# Revit family: Hager-PEDRO-Surface_mounted-IP66-With_Cover-With_DIN-NoHosted-IT-it
name_source: partatom
category: Electrical Equipment
units: mm (PartAtom-declared; Revit-internal decimal feet)

## family parameters
Always vertical = Yes
Cut with Voids When Loaded = No
Maintain Annotation Orientation = No
Panel Configuration = Two Columns, Circuits Across
Part Type = Panelboard
Room Calculation Point = No
Round Connector Dimension = Use Diameter
Shared = No
Work Plane-Based = Yes

## types (26) — shared parameters
Code hager = ADD-EC000214_EU
Default Elevation = 1200 mm
EF000003 - Tipo di montaggio = A parete
EF000007 - Colore = Grigio
EF000024 - Resistente ai raggi UV = No
EF000116 - Numero RAL = 7035
EF000118 - Con piastra di montaggio = No
EF001062 - Esecuzione EMC = Yes
EF001088 - Possibilità di applicazione = Yes
EF001134 - Barra DIN = Yes
EF004462 - Tipo di chiusura = Altro
EF005474 - Grado di protezione (IP) = IP66
EF006306 - Con serratura = Yes
EF009212 - Esecuzione coperchio = Chiuso
EF015776 - Morsettiera di terra = No
EF015777 - Morsettiera neutra = No
EF015941 - Segnale di passaggio porta = No
ETIM class code = EC000214
ETIM class name = Small distribution board
HG000002-with door or cover-it = Yes
HG000003-Range-it = PEDRO
HG000005-Thickness-it = 2 mm  [stored 0.00656168 ft]
HG000006-Flush mounted-it = No
HG000009-Double swing door-it = No
HG000010-Asymmetric doors-it = No
HG000011-Empty rows from bottom-it = No
HG000012-Door swing angle-it = 90.00°
HG000013-Door on the left-it = No
HG000014-Door on the right-it = Yes
HG000015-Clearance visibility-it = Yes
HG000016-Door 3D visibility-it = Yes
HG000017-Distance between poles-it = 18 mm  [stored 0.0590551 ft]
HG000060-RAL-number = 7035
HG000099-Onfly Template ID-it-IT = 507532
Manufacturer = Hager
Name BIM&CO = Electricity
Name hager = ADD_Enclosures_EC000214
Reference = Template-Enclosure_EU-EC000214
Uniformat = Low Tension Service & Dist.
Uniformat code = D501001
zero-valued in all types: EF000218 - Profondità di incasso, EF000332 - Altezza della parte incassata, EF000846 - Larghezza di montaggio, EF001131 - Profondità interna, HG000007-Number of empty columns-it, HG000008-Number of empty rows-it

## per-type parameters (varying)
| type | BC_METADATA | EF000008 - Larghezza | EF000040 - Altezza | EF000049 - Profondità | EF000266 - Numero di file | EF002950 - Numero moduli DIN | EF006244 - Coperchio/porta trasparente | HG000001 - Numero di colonne | HG000004-Manufacturer reference-it | HGEF000266-Numero di file | HGEF0002950-Numero moduli DIN |
| PEDRO-Surface_mounted_W265_H303_D167_0_Modular_Spacing-B04601 | {"ObjectGuid":"712c051a-f6a5-42ba-8971-c6f35d6c2ee9","ModelGuid":"f9864149-d723-4e03-9b42-689d61447cad","VariantGuid":"83e1c283-c7cc-4c8f-adfe-bcd37362c99a","Revision":"#6","VariantName":"PEDRO-Surface_mounted_W265_H303_D167_0_Modular_Spacing-B04601"} | 265 mm  [stored 0.869423 ft] | 303 mm  [stored 0.994094 ft] | 167 mm  [stored 0.5479 ft] | 0 | 0 | No | 0 | B04601 | 0 | 0 |
| PEDRO-Surface_mounted_W325_H428_D178_12_Modular_Spacing-B04602 | {"ObjectGuid":"712c051a-f6a5-42ba-8971-c6f35d6c2ee9","ModelGuid":"f9864149-d723-4e03-9b42-689d61447cad","VariantGuid":"5e6dea64-c1f4-491c-8259-0979995b25e5","Revision":"#6","VariantName":"PEDRO-Surface_mounted_W325_H428_D178_12_Modular_Spacing-B04602"} | 325 mm  [stored 1.06627 ft] | 428 mm  [stored 1.4042 ft] | 178 mm  [stored 0.58399 ft] | 3 | 12 | No | 1 | B04602 | 3 | 12 |
| PEDRO-Surface_mounted_W433.5_H504_D210_18_Modular_Spacing-B04603 | {"ObjectGuid":"712c051a-f6a5-42ba-8971-c6f35d6c2ee9","ModelGuid":"f9864149-d723-4e03-9b42-689d61447cad","VariantGuid":"90c5386f-695a-4bef-bba7-171966b9a392","Revision":"#6","VariantName":"PEDRO-Surface_mounted_W433.5_H504_D210_18_Modular_Spacing-B04603"} | 434 mm  [stored 1.42388 ft] | 504 mm  [stored 1.65354 ft] | 210 mm  [stored 0.688976 ft] | 3 | 18 | No | 1 | B04603 | 3 | 18 |
| PEDRO-Surface_mounted_W433.5_H654_D210_18_Modular_Spacing-B04604 | {"ObjectGuid":"712c051a-f6a5-42ba-8971-c6f35d6c2ee9","ModelGuid":"f9864149-d723-4e03-9b42-689d61447cad","VariantGuid":"bd4542a3-c377-4a03-a8b2-04f1ed40170a","Revision":"#6","VariantName":"PEDRO-Surface_mounted_W433.5_H654_D210_18_Modular_Spacing-B04604"} | 434 mm  [stored 1.42388 ft] | 654 mm | 210 mm  [stored 0.688976 ft] | 4 | 18 | No | 1 | B04604 | 4 | 18 |
| PEDRO-Surface_mounted_W543_H654_D265_24_Modular_Spacing-B04605 | {"ObjectGuid":"712c051a-f6a5-42ba-8971-c6f35d6c2ee9","ModelGuid":"f9864149-d723-4e03-9b42-689d61447cad","VariantGuid":"9e8eceff-b8b6-4340-8496-66e8dd6d7c78","Revision":"#6","VariantName":"PEDRO-Surface_mounted_W543_H654_D265_24_Modular_Spacing-B04605"} | 543 mm  [stored 1.7815 ft] | 654 mm | 265 mm  [stored 0.869423 ft] | 4 | 24 | No | 1 | B04605 | 4 | 24 |
| PEDRO-Surface_mounted_W615.4_H806_D318.7_28_Modular_Spacing-B04606 | {"ObjectGuid":"712c051a-f6a5-42ba-8971-c6f35d6c2ee9","ModelGuid":"f9864149-d723-4e03-9b42-689d61447cad","VariantGuid":"0de67e4e-3713-413f-bf4a-b1da15a99b19","Revision":"#6","VariantName":"PEDRO-Surface_mounted_W615.4_H806_D318.7_28_Modular_Spacing-B04606"} | 615 mm | 806 mm  [stored 2.64436 ft] | 319 mm  [stored 1.04659 ft] | 5 | 28 | No | 1 | B04606 | 5 | 28 |
| PEDRO-Surface_mounted_W810_H1056_D355_38_Modular_Spacing-B04608 | {"ObjectGuid":"712c051a-f6a5-42ba-8971-c6f35d6c2ee9","ModelGuid":"f9864149-d723-4e03-9b42-689d61447cad","VariantGuid":"d5d3cacc-da2b-44ad-87fb-499da4fe861c","Revision":"#6","VariantName":"PEDRO-Surface_mounted_W810_H1056_D355_38_Modular_Spacing-B04608"} | 810 mm | 1056 mm  [stored 3.46457 ft] | 355 mm | 5 | 38 | No | 1 | B04608 | 5 | 38 |
| PEDRO-Surface_mounted_W265_H303_D167_0_Modular_Spacing-B04621 | {"ObjectGuid":"712c051a-f6a5-42ba-8971-c6f35d6c2ee9","ModelGuid":"f9864149-d723-4e03-9b42-689d61447cad","VariantGuid":"6485a578-a258-471d-afc4-453fd7a044a0","Revision":"#6","VariantName":"PEDRO-Surface_mounted_W265_H303_D167_0_Modular_Spacing-B04621"} | 265 mm  [stored 0.869423 ft] | 303 mm  [stored 0.994094 ft] | 167 mm  [stored 0.5479 ft] | 0 | 0 | Yes | 0 | B04621 | 0 | 0 |
| PEDRO-Surface_mounted_W325_H428_D183_12_Modular_Spacing-B04622 | {"ObjectGuid":"712c051a-f6a5-42ba-8971-c6f35d6c2ee9","ModelGuid":"f9864149-d723-4e03-9b42-689d61447cad","VariantGuid":"f4cc03e8-5788-4a50-b014-92ac4e830229","Revision":"#6","VariantName":"PEDRO-Surface_mounted_W325_H428_D183_12_Modular_Spacing-B04622"} | 325 mm  [stored 1.06627 ft] | 428 mm  [stored 1.4042 ft] | 183 mm | 3 | 12 | Yes | 1 | B04622 | 3 | 12 |
| PEDRO-Surface_mounted_W434_H504_D210_18_Modular_Spacing-B04623 | {"ObjectGuid":"712c051a-f6a5-42ba-8971-c6f35d6c2ee9","ModelGuid":"f9864149-d723-4e03-9b42-689d61447cad","VariantGuid":"3269d936-6ee5-4c32-9a7e-7dfc4a4c7b15","Revision":"#6","VariantName":"PEDRO-Surface_mounted_W434_H504_D210_18_Modular_Spacing-B04623"} | 434 mm  [stored 1.42388 ft] | 504 mm  [stored 1.65354 ft] | 210 mm  [stored 0.688976 ft] | 3 | 18 | Yes | 1 | B04623 | 3 | 18 |
| PEDRO-Surface_mounted_W434_H654_D210_18_Modular_Spacing-B04624 | {"ObjectGuid":"712c051a-f6a5-42ba-8971-c6f35d6c2ee9","ModelGuid":"f9864149-d723-4e03-9b42-689d61447cad","VariantGuid":"5db9bc35-a5ae-4cd9-a359-3bd38e1c99b3","Revision":"#6","VariantName":"PEDRO-Surface_mounted_W434_H654_D210_18_Modular_Spacing-B04624"} | 434 mm  [stored 1.42388 ft] | 654 mm | 210 mm  [stored 0.688976 ft] | 4 | 18 | Yes | 1 | B04624 | 4 | 18 |
| PEDRO-Surface_mounted_W543_H654_D265_24_Modular_Spacing-B04625 | {"ObjectGuid":"712c051a-f6a5-42ba-8971-c6f35d6c2ee9","ModelGuid":"f9864149-d723-4e03-9b42-689d61447cad","VariantGuid":"3d92ce08-3b62-42e5-bbdf-84b2c4f34e4e","Revision":"#6","VariantName":"PEDRO-Surface_mounted_W543_H654_D265_24_Modular_Spacing-B04625"} | 543 mm  [stored 1.7815 ft] | 654 mm | 265 mm  [stored 0.869423 ft] | 4 | 24 | Yes | 1 | B04625 | 4 | 24 |
| PEDRO-Surface_mounted_W616_H806_D319_28_Modular_Spacing-B04626 | {"ObjectGuid":"712c051a-f6a5-42ba-8971-c6f35d6c2ee9","ModelGuid":"f9864149-d723-4e03-9b42-689d61447cad","VariantGuid":"4088d2d8-4f38-4d24-ab03-d1aaa88ef20d","Revision":"#6","VariantName":"PEDRO-Surface_mounted_W616_H806_D319_28_Modular_Spacing-B04626"} | 616 mm  [stored 2.021 ft] | 806 mm  [stored 2.64436 ft] | 319 mm  [stored 1.04659 ft] | 5 | 28 | Yes | 1 | B04626 | 5 | 28 |
| PEDRO-Surface_mounted_W810_H1056_D355_38_Modular_Spacing-B04628 | {"ObjectGuid":"712c051a-f6a5-42ba-8971-c6f35d6c2ee9","ModelGuid":"f9864149-d723-4e03-9b42-689d61447cad","VariantGuid":"39e0b71c-3581-4bf3-97ac-8f3fca45593a","Revision":"#6","VariantName":"PEDRO-Surface_mounted_W810_H1056_D355_38_Modular_Spacing-B04628"} | 810 mm | 1056 mm  [stored 3.46457 ft] | 355 mm | 5 | 38 | Yes | 1 | B04628 | 5 | 38 |
| PEDRO-Surface_mounted_W325_H428_D183_12_Modular_Spacing-B04712 | {"ObjectGuid":"712c051a-f6a5-42ba-8971-c6f35d6c2ee9","ModelGuid":"f9864149-d723-4e03-9b42-689d61447cad","VariantGuid":"b67c811a-b318-4c09-be37-653ad378c423","Revision":"#6","VariantName":"PEDRO-Surface_mounted_W325_H428_D183_12_Modular_Spacing-B04712"} | 325 mm  [stored 1.06627 ft] | 428 mm  [stored 1.4042 ft] | 183 mm | 3 | 12 | No | 1 | B04712 | 3 | 12 |
| PEDRO-Surface_mounted_W434_H504_D210_18_Modular_Spacing-B04713 | {"ObjectGuid":"712c051a-f6a5-42ba-8971-c6f35d6c2ee9","ModelGuid":"f9864149-d723-4e03-9b42-689d61447cad","VariantGuid":"52a7278d-0b82-4942-b5f9-d7a94ad146e9","Revision":"#6","VariantName":"PEDRO-Surface_mounted_W434_H504_D210_18_Modular_Spacing-B04713"} | 434 mm  [stored 1.42388 ft] | 504 mm  [stored 1.65354 ft] | 210 mm  [stored 0.688976 ft] | 3 | 18 | No | 0 | B04713 | 3 | 18 |
| PEDRO-Surface_mounted_W434_H650_D210_18_Modular_Spacing-B04714 | {"ObjectGuid":"712c051a-f6a5-42ba-8971-c6f35d6c2ee9","ModelGuid":"f9864149-d723-4e03-9b42-689d61447cad","VariantGuid":"734289a9-2675-4ff8-9a43-7696deae559b","Revision":"#6","VariantName":"PEDRO-Surface_mounted_W434_H650_D210_18_Modular_Spacing-B04714"} | 434 mm  [stored 1.42388 ft] | 650 mm  [stored 2.13255 ft] | 210 mm  [stored 0.688976 ft] | 4 | 18 | No | 0 | B04714 | 4 | 18 |
| PEDRO-Surface_mounted_W543_H654_D265_24_Modular_Spacing-B04715 | {"ObjectGuid":"712c051a-f6a5-42ba-8971-c6f35d6c2ee9","ModelGuid":"f9864149-d723-4e03-9b42-689d61447cad","VariantGuid":"e5e7792e-bb49-4e84-99fb-72b7b6e85006","Revision":"#6","VariantName":"PEDRO-Surface_mounted_W543_H654_D265_24_Modular_Spacing-B04715"} | 543 mm  [stored 1.7815 ft] | 654 mm | 265 mm  [stored 0.869423 ft] | 4 | 24 | No | 0 | B04715 | 4 | 24 |
| PEDRO-Surface_mounted_W616_H806_D319_28_Modular_Spacing-B04716 | {"ObjectGuid":"712c051a-f6a5-42ba-8971-c6f35d6c2ee9","ModelGuid":"f9864149-d723-4e03-9b42-689d61447cad","VariantGuid":"c1d8f227-a4c1-40c5-a27d-934802c3a74f","Revision":"#6","VariantName":"PEDRO-Surface_mounted_W616_H806_D319_28_Modular_Spacing-B04716"} | 616 mm  [stored 2.021 ft] | 806 mm  [stored 2.64436 ft] | 319 mm  [stored 1.04659 ft] | 5 | 28 | No | 0 | B04716 | 5 | 28 |
| PEDRO-Surface_mounted_W810_H1056_D355_38_Modular_Spacing-B04717 | {"ObjectGuid":"712c051a-f6a5-42ba-8971-c6f35d6c2ee9","ModelGuid":"f9864149-d723-4e03-9b42-689d61447cad","VariantGuid":"6fa415ec-c034-459e-a9f3-d986c31e19ba","Revision":"#6","VariantName":"PEDRO-Surface_mounted_W810_H1056_D355_38_Modular_Spacing-B04717"} | 810 mm | 1056 mm  [stored 3.46457 ft] | 355 mm | 5 | 38 | No | 0 | B04717 | 5 | 38 |
| PEDRO-Surface_mounted_W325_H428_D183_12_Modular_Spacing-B04722 | {"ObjectGuid":"712c051a-f6a5-42ba-8971-c6f35d6c2ee9","ModelGuid":"f9864149-d723-4e03-9b42-689d61447cad","VariantGuid":"a79e5a93-9976-4cf4-8b57-a08a7f80257f","Revision":"#6","VariantName":"PEDRO-Surface_mounted_W325_H428_D183_12_Modular_Spacing-B04722"} | 325 mm  [stored 1.06627 ft] | 428 mm  [stored 1.4042 ft] | 183 mm | 3 | 12 | Yes | 1 | B04722 | 3 | 12 |
| PEDRO-Surface_mounted_W434_H504_D210_18_Modular_Spacing-B04723 | {"ObjectGuid":"712c051a-f6a5-42ba-8971-c6f35d6c2ee9","ModelGuid":"f9864149-d723-4e03-9b42-689d61447cad","VariantGuid":"e7e18a2f-7f0a-4c22-8c83-fb895b2decf8","Revision":"#6","VariantName":"PEDRO-Surface_mounted_W434_H504_D210_18_Modular_Spacing-B04723"} | 434 mm  [stored 1.42388 ft] | 504 mm  [stored 1.65354 ft] | 210 mm  [stored 0.688976 ft] | 3 | 18 | Yes | 0 | B04723 | 3 | 18 |
| PEDRO-Surface_mounted_W434_H654_D210_18_Modular_Spacing-B04724 | {"ObjectGuid":"712c051a-f6a5-42ba-8971-c6f35d6c2ee9","ModelGuid":"f9864149-d723-4e03-9b42-689d61447cad","VariantGuid":"bff4ae68-42ff-4f9c-8c7d-ac243393b91b","Revision":"#6","VariantName":"PEDRO-Surface_mounted_W434_H654_D210_18_Modular_Spacing-B04724"} | 434 mm  [stored 1.42388 ft] | 654 mm | 210 mm  [stored 0.688976 ft] | 4 | 18 | Yes | 0 | B04724 | 4 | 18 |
| PEDRO-Surface_mounted_W543_H654_D265_24_Modular_Spacing-B04725 | {"ObjectGuid":"712c051a-f6a5-42ba-8971-c6f35d6c2ee9","ModelGuid":"f9864149-d723-4e03-9b42-689d61447cad","VariantGuid":"48b5e2a0-a50c-4e54-865a-8d5780a424f1","Revision":"#6","VariantName":"PEDRO-Surface_mounted_W543_H654_D265_24_Modular_Spacing-B04725"} | 543 mm  [stored 1.7815 ft] | 654 mm | 265 mm  [stored 0.869423 ft] | 4 | 24 | Yes | 0 | B04725 | 4 | 24 |
| PEDRO-Surface_mounted_W616_H806_D319_28_Modular_Spacing-B04726 | {"ObjectGuid":"712c051a-f6a5-42ba-8971-c6f35d6c2ee9","ModelGuid":"f9864149-d723-4e03-9b42-689d61447cad","VariantGuid":"d27e814a-4c42-4bf2-85d1-99ada70bbcec","Revision":"#6","VariantName":"PEDRO-Surface_mounted_W616_H806_D319_28_Modular_Spacing-B04726"} | 616 mm  [stored 2.021 ft] | 806 mm  [stored 2.64436 ft] | 319 mm  [stored 1.04659 ft] | 5 | 28 | Yes | 0 | B04726 | 5 | 28 |
| PEDRO-Surface_mounted_W810_H1056_D355_38_Modular_Spacing-B04727 | {"ObjectGuid":"712c051a-f6a5-42ba-8971-c6f35d6c2ee9","ModelGuid":"f9864149-d723-4e03-9b42-689d61447cad","VariantGuid":"3fda5a05-6260-466f-9934-a724d2a1f99a","Revision":"#6","VariantName":"PEDRO-Surface_mounted_W810_H1056_D355_38_Modular_Spacing-B04727"} | 810 mm | 1056 mm  [stored 3.46457 ft] | 355 mm | 5 | 38 | Yes | 0 | B04727 | 5 | 38 |

note: [stored X ft] marks values corroborated as IEEE doubles in the binary element streams (Revit-internal decimal feet)

## geometry (parser evidence)
native form markers: Sweep x14
no freeform markers — native parametric forms only
